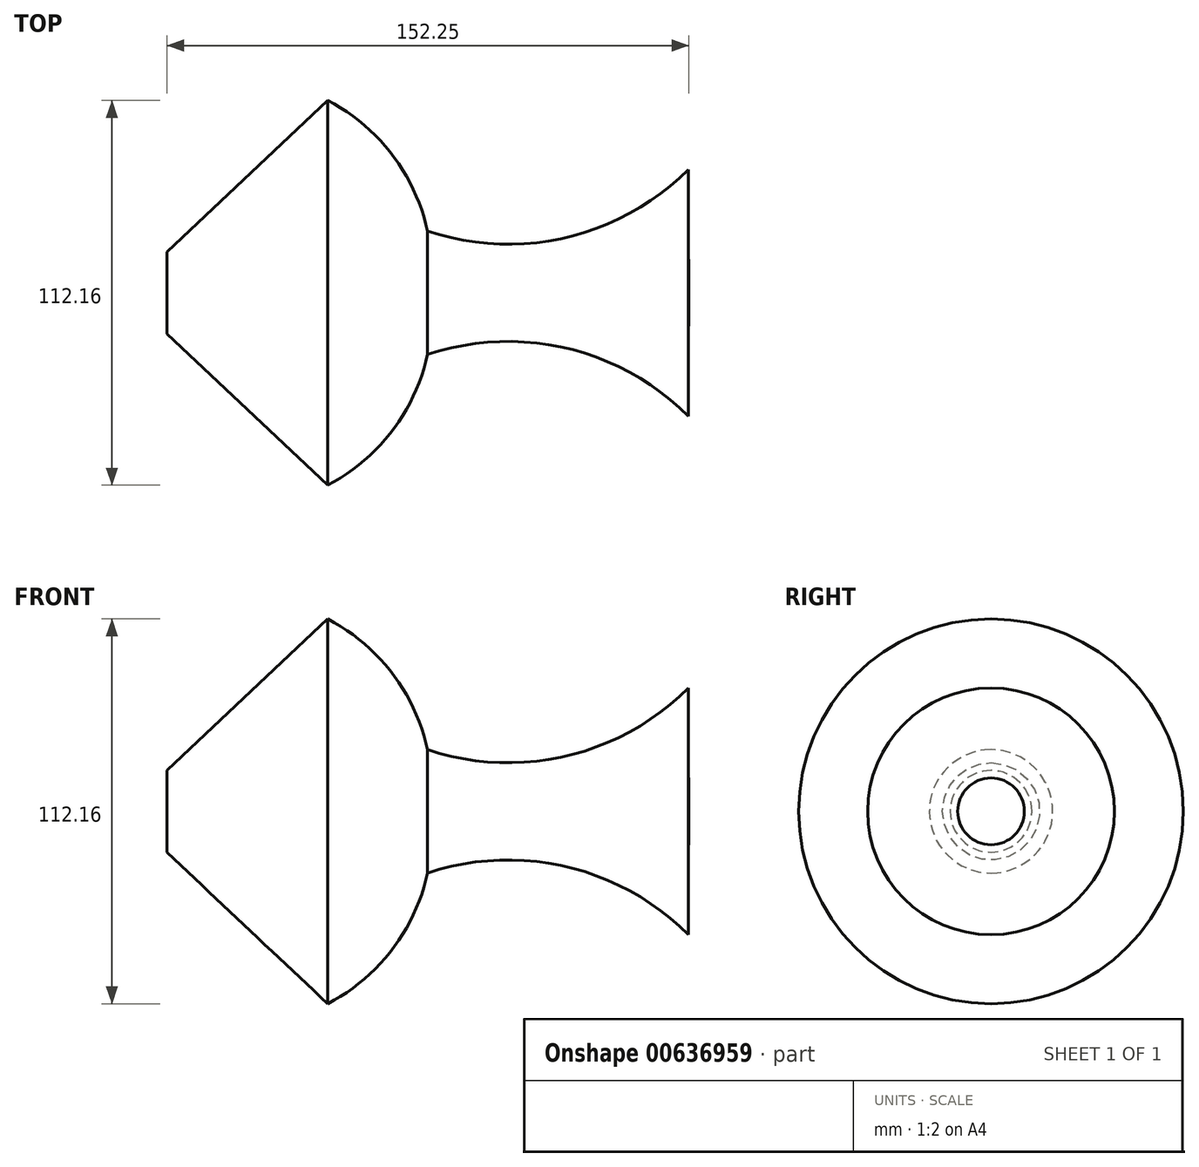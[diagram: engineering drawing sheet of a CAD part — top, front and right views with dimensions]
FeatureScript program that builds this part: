
annotation { "Feature Type Name" : "Feature", "Feature Type Description" : "" }
export const myFeature = defineFeature(function(context is Context, id is Id, definition is map)
    precondition{}
    {
        {
            var Q0;
            Q0=qCreatedBy(makeId("Right.planeOp"),FACE);
            var sketch = newSketch(context, id + "F0", { "sketchPlane" : qUnion([Q0])});
            skCircle(sketch, "E0", {"center": v(0, 0) * mm, "radius": 9.73 * mm});
            skSolve(sketch);
        }
        {
            var Q0;
            Q0=makeQuery(id+"F0.imprint","IMPRINT",FACE,{"disambiguationData":[TD([[makeQuery(id+"F0.imprint","IMPRINT",EDGE,{"derivedFrom":sQuery(id+"F0.wireOp",EDGE,"E0")}),1.0]])]});
            extrude(context, id + "F1", {"entities" : qUnion([Q0]), "depth" : 76.2 * mm, "offsetDistance" : 25.4 * mm, "hasSecondDirection" : true, "secondDirectionOppositeDirection" : true, "secondDirectionDepth" : 76.2 * mm});
        }
        {
            var Q0;
            Q0=qCreatedBy(makeId("Front.planeOp"),FACE);
            var sketch = newSketch(context, id + "F2", { "sketchPlane" : qUnion([Q0])});
            skLineSegment(sketch, "E1", {"start": v(0, 0) * mm, "end": v(0, 17.98) * mm});
            skLineSegment(sketch, "E2", {"start": v(0, 0) * mm, "end": v(-76.05, 0) * mm});
            skLineSegment(sketch, "E3", {"start": v(-76.05, 0) * mm, "end": v(-76.05, 11.9) * mm});
            skLineSegment(sketch, "E4", {"start": v(-76.05, 11.9) * mm, "end": v(-29.1, 56.08) * mm});
            skLineSegment(sketch, "E5", {"start": v(-29.1, 56.08) * mm, "end": v(-29.1, 20.42) * mm});
            skLineSegment(sketch, "E6", {"start": v(-29.1, 20.42) * mm, "end": v(0, 17.98) * mm});
            skPoint(sketch, "E7.MirrorCS.end.orphan", {"position": v(0, 17.98) * mm});
            skPoint(sketch, "E7.MirrorCS.start.orphan", {"position": v(29.1, 20.42) * mm});
            skPoint(sketch, "E8.MirrorCS.start.orphan", {"position": v(29.1, 56.08) * mm});
            skPoint(sketch, "E9.MirrorCS.start.orphan", {"position": v(76.05, 11.9) * mm});
            skPoint(sketch, "E10.MirrorCS.start.orphan", {"position": v(76.05, 0) * mm});
            skPoint(sketch, "E11.MirrorCS.start.orphan", {"position": v(0, 0) * mm});
            skLineSegment(sketch, "E12", {"start": v(76.05, 0) * mm, "end": v(76.05, 35.97) * mm});
            skArc(sketch, "E13", {"start": v(0, 17.98) * mm, "mid": v(40.58, 16.16) * mm, "end": v(76.05, 35.97) * mm});
            skLineSegment(sketch, "E14", {"start": v(0, 0) * mm, "end": v(76.05, 0) * mm});
            skArc(sketch, "E15", {"start": v(0, 17.98) * mm, "mid": v(-10.34, 40.25) * mm, "end": v(-29.1, 56.08) * mm});
            skLineSegment(sketch, "E16", {"start": v(-76.05, 0) * mm, "end": v(-111.7, 0) * mm});
            skArc(sketch, "E17", {"start": v(-111.7, 0) * mm, "mid": v(-92.91, 3.05) * mm, "end": v(-76.05, 11.9) * mm});
            skSolve(sketch);
        }
        {
            var Q0;
            Q0=makeQuery(id+"F2.imprint","IMPRINT",FACE,{"disambiguationData":[TD([[makeQuery(id+"F2.imprint","IMPRINT",EDGE,{"derivedFrom":sQuery(id+"F2.wireOp",EDGE,"E1")}),1.0]])]});
            var Q1;
            Q1=sQuery(id+"F2.wireOp",EDGE,"E2");
            revolve(context, id + "F3", {"operationType" : NewBodyOperationType.ADD, "entities" : qUnion([Q0]), "axis" : qUnion([Q1]), "revolveType" : RevolveType.FULL});
        }
        {
            var Q0;
            Q0=makeQuery(id+"F2.imprint","IMPRINT",FACE,{"disambiguationData":[TD([[makeQuery(id+"F2.imprint","IMPRINT",EDGE,{"derivedFrom":sQuery(id+"F2.wireOp",EDGE,"E1")}),-1.0]])]});
            var Q1;
            Q1=sQuery(id+"F2.wireOp",EDGE,"E14");
            revolve(context, id + "F4", {"operationType" : NewBodyOperationType.ADD, "entities" : qUnion([Q0]), "axis" : qUnion([Q1]), "revolveType" : RevolveType.FULL});
        }
        {
            var Q0;
            Q0=makeQuery(id+"F2.imprint","IMPRINT",FACE,{"disambiguationData":[TD([[makeQuery(id+"F2.imprint","IMPRINT",EDGE,{"derivedFrom":sQuery(id+"F2.wireOp",EDGE,"E5")}),1.0]])]});
            var Q1;
            Q1=sQuery(id+"F2.wireOp",EDGE,"E2");
            revolve(context, id + "F5", {"operationType" : NewBodyOperationType.ADD, "entities" : qUnion([Q0]), "axis" : qUnion([Q1]), "revolveType" : RevolveType.FULL});
        }
        {
            var Q0;
            Q0=makeQuery(id+"F2.imprint","IMPRINT",FACE,{"disambiguationData":[TD([[makeQuery(id+"F2.imprint","IMPRINT",EDGE,{"derivedFrom":sQuery(id+"F2.wireOp",EDGE,"E3")}),1.0]])]});
            var Q1;
            Q1=sQuery(id+"F2.wireOp",EDGE,"E2");
            revolve(context, id + "F6", {"operationType" : NewBodyOperationType.ADD, "entities" : qUnion([Q0]), "axis" : qUnion([Q1]), "revolveType" : RevolveType.FULL});
        }
    });
